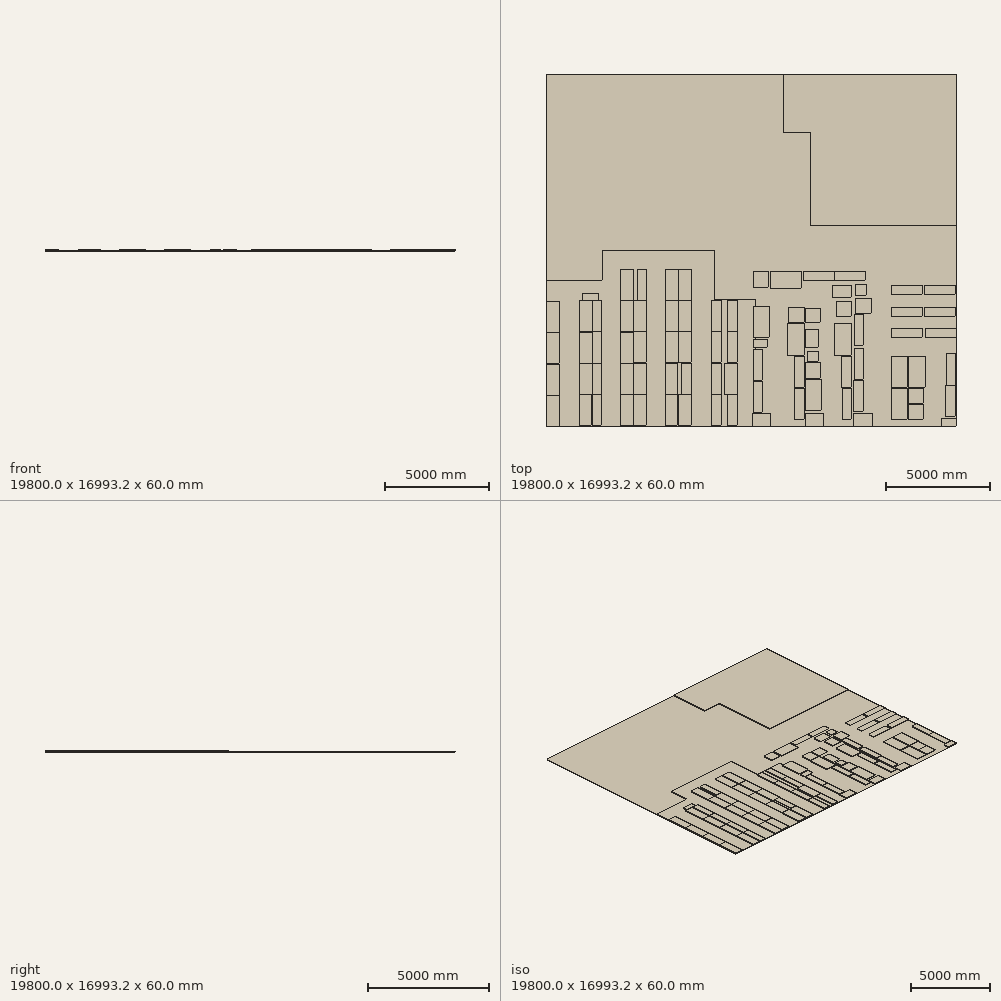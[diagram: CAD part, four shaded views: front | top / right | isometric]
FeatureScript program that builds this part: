
annotation { "Feature Type Name" : "Feature", "Feature Type Description" : "" }
export const myFeature = defineFeature(function(context is Context, id is Id, definition is map)
    precondition{}
    {
        {
            var Q0;
            Q0=qCreatedBy(makeId("Top.planeOp"),FACE);
            var sketch = newSketch(context, id + "F0", { "sketchPlane" : qUnion([Q0])});
            skLineSegment(sketch, "E0.bottom", {"start": v(9900, -8495) * mm, "end": v(-9900, -8495) * mm});
            skLineSegment(sketch, "E0.top", {"start": v(9900, 8495) * mm, "end": v(-9900, 8495) * mm});
            skLineSegment(sketch, "E0.left", {"start": v(9900, -8495) * mm, "end": v(9900, 8495) * mm});
            skLineSegment(sketch, "E0.right", {"start": v(-9900, -8495) * mm, "end": v(-9900, 8495) * mm});
            skPoint(sketch, "E0.middle", {"position": v(0, 0) * mm});
            skSolve(sketch);
        }
        {
            var Q0;
            Q0=qSketchRegion(id+"F0",true);
            extrude(context, id + "F1", {"entities" : qUnion([Q0]), "depth" : 10 * mm});
        }
        {
            var Q0;
            Q0=makeQuery(id+"F1.opExtrude","CAP_FACE",FACE,{"disambiguationData":[OSD([sQuery(id+"F0.wireOp",EDGE,"E0.bottom"),sQuery(id+"F0.wireOp",EDGE,"E0.top"),sQuery(id+"F0.wireOp",EDGE,"E0.left"),sQuery(id+"F0.wireOp",EDGE,"E0.right")])],"isStart":false});
            var sketch = newSketch(context, id + "F2", { "sketchPlane" : qUnion([Q0])});
            skLineSegment(sketch, "E1", {"start": v(-9900, -8495) * mm, "end": v(-9900, -1435) * mm});
            skLineSegment(sketch, "E2", {"start": v(-9900, -1435) * mm, "end": v(-7200, -1435) * mm});
            skLineSegment(sketch, "E3", {"start": v(-7200, -1435) * mm, "end": v(-7200, -5) * mm});
            skLineSegment(sketch, "E4", {"start": v(-7200, -5) * mm, "end": v(-1800, -5) * mm});
            skLineSegment(sketch, "E5", {"start": v(-1800, -5) * mm, "end": v(-1800, -2355) * mm});
            skLineSegment(sketch, "E6", {"start": v(-1800, -2355) * mm, "end": v(200, -2355) * mm});
            skLineSegment(sketch, "E7", {"start": v(200, -2355) * mm, "end": v(200, -8495) * mm});
            skLineSegment(sketch, "E8", {"start": v(200, -8495) * mm, "end": v(-9900, -8495) * mm});
            skLineSegment(sketch, "E9", {"start": v(9900, 1195) * mm, "end": v(9900, 8495) * mm});
            skLineSegment(sketch, "E10", {"start": v(9900, 8495) * mm, "end": v(1550, 8495) * mm});
            skLineSegment(sketch, "E11", {"start": v(1550, 8495) * mm, "end": v(1550, 5715) * mm});
            skLineSegment(sketch, "E12", {"start": v(1550, 5715) * mm, "end": v(2850, 5715) * mm});
            skLineSegment(sketch, "E13", {"start": v(2850, 5715) * mm, "end": v(2850, 1195) * mm});
            skLineSegment(sketch, "E14", {"start": v(2850, 1195) * mm, "end": v(9900, 1195) * mm});
            skLineSegment(sketch, "E15.left", {"start": v(3458.32, 469.72) * mm, "end": v(3008.32, 469.72) * mm});
            skPoint(sketch, "E15.middle", {"position": v(3233.32, -280.28) * mm});
            skLineSegment(sketch, "E16.left", {"start": v(4716.05, -36.44) * mm, "end": v(4096.05, -36.44) * mm});
            skPoint(sketch, "E16.middle", {"position": v(4406.05, -786.44) * mm});
            skSolve(sketch);
        }
        {
            var Q0;
            Q0=qSketchRegion(id+"F2",true);
            extrude(context, id + "F3", {"entities" : qUnion([Q0]), "operationType" : NewBodyOperationType.ADD, "depth" : 25 * mm});
        }
        {
            var Q0;
            Q0=makeQuery(id+"F3.opExtrude","CAP_FACE",FACE,{"disambiguationData":[OSD([sQuery(id+"F2.wireOp",EDGE,"E1"),sQuery(id+"F2.wireOp",EDGE,"E2"),sQuery(id+"F2.wireOp",EDGE,"E3"),sQuery(id+"F2.wireOp",EDGE,"E4"),sQuery(id+"F2.wireOp",EDGE,"E5"),sQuery(id+"F2.wireOp",EDGE,"E6"),sQuery(id+"F2.wireOp",EDGE,"E7"),sQuery(id+"F2.wireOp",EDGE,"E8")])],"isStart":false});
            var sketch = newSketch(context, id + "F4", { "sketchPlane" : qUnion([Q0])});
            skLineSegment(sketch, "E17.bottom", {"start": v(-9900, -8495) * mm, "end": v(-9900, -6995) * mm});
            skLineSegment(sketch, "E17.top", {"start": v(-9280, -8495) * mm, "end": v(-9280, -6995) * mm});
            skLineSegment(sketch, "E17.left", {"start": v(-9900, -8495) * mm, "end": v(-9280, -8495) * mm});
            skLineSegment(sketch, "E17.right", {"start": v(-9900, -6995) * mm, "end": v(-9280, -6995) * mm});
            skPoint(sketch, "E17.middle", {"position": v(-9590, -7745) * mm});
            skLineSegment(sketch, "E18.bottom", {"start": v(-9892.84, -6987.42) * mm, "end": v(-9892.84, -5487.42) * mm});
            skLineSegment(sketch, "E18.top", {"start": v(-9272.84, -6987.42) * mm, "end": v(-9272.84, -5487.42) * mm});
            skLineSegment(sketch, "E18.left", {"start": v(-9892.84, -6987.42) * mm, "end": v(-9272.84, -6987.42) * mm});
            skLineSegment(sketch, "E18.right", {"start": v(-9892.84, -5487.42) * mm, "end": v(-9272.84, -5487.42) * mm});
            skPoint(sketch, "E18.middle", {"position": v(-9582.84, -6237.42) * mm});
            skLineSegment(sketch, "E19.bottom", {"start": v(-9892.84, -5474.56) * mm, "end": v(-9892.84, -3974.56) * mm});
            skLineSegment(sketch, "E19.top", {"start": v(-9272.84, -5474.56) * mm, "end": v(-9272.84, -3974.56) * mm});
            skLineSegment(sketch, "E19.left", {"start": v(-9892.84, -5474.56) * mm, "end": v(-9272.84, -5474.56) * mm});
            skLineSegment(sketch, "E19.right", {"start": v(-9892.84, -3974.56) * mm, "end": v(-9272.84, -3974.56) * mm});
            skPoint(sketch, "E19.middle", {"position": v(-9582.84, -4724.56) * mm});
            skLineSegment(sketch, "E20.bottom", {"start": v(-9892.84, -3964.29) * mm, "end": v(-9892.84, -2464.29) * mm});
            skLineSegment(sketch, "E20.top", {"start": v(-9272.84, -3964.29) * mm, "end": v(-9272.84, -2464.29) * mm});
            skLineSegment(sketch, "E20.left", {"start": v(-9892.84, -3964.29) * mm, "end": v(-9272.84, -3964.29) * mm});
            skLineSegment(sketch, "E20.right", {"start": v(-9892.84, -2464.29) * mm, "end": v(-9272.84, -2464.29) * mm});
            skPoint(sketch, "E20.middle", {"position": v(-9582.84, -3214.29) * mm});
            skLineSegment(sketch, "E21.bottom", {"start": v(-8329.6, -8467.89) * mm, "end": v(-8329.6, -6967.89) * mm});
            skLineSegment(sketch, "E21.top", {"start": v(-7709.6, -8467.89) * mm, "end": v(-7709.6, -6967.89) * mm});
            skLineSegment(sketch, "E21.left", {"start": v(-8329.6, -8467.89) * mm, "end": v(-7709.6, -8467.89) * mm});
            skLineSegment(sketch, "E21.right", {"start": v(-8329.6, -6967.89) * mm, "end": v(-7709.6, -6967.89) * mm});
            skPoint(sketch, "E21.middle", {"position": v(-8019.6, -7717.89) * mm});
            skLineSegment(sketch, "E22.bottom", {"start": v(-8322.44, -6960.31) * mm, "end": v(-8322.44, -5460.31) * mm});
            skLineSegment(sketch, "E22.top", {"start": v(-7702.44, -6960.31) * mm, "end": v(-7702.44, -5460.31) * mm});
            skLineSegment(sketch, "E22.left", {"start": v(-8322.44, -6960.31) * mm, "end": v(-7702.44, -6960.31) * mm});
            skLineSegment(sketch, "E22.right", {"start": v(-8322.44, -5460.31) * mm, "end": v(-7702.44, -5460.31) * mm});
            skPoint(sketch, "E22.middle", {"position": v(-8012.44, -6210.31) * mm});
            skLineSegment(sketch, "E23.bottom", {"start": v(-8322.44, -5447.45) * mm, "end": v(-8322.44, -3947.45) * mm});
            skLineSegment(sketch, "E23.top", {"start": v(-7702.44, -5447.45) * mm, "end": v(-7702.44, -3947.45) * mm});
            skLineSegment(sketch, "E23.left", {"start": v(-8322.44, -5447.45) * mm, "end": v(-7702.44, -5447.45) * mm});
            skLineSegment(sketch, "E23.right", {"start": v(-8322.44, -3947.45) * mm, "end": v(-7702.44, -3947.45) * mm});
            skPoint(sketch, "E23.middle", {"position": v(-8012.44, -4697.45) * mm});
            skLineSegment(sketch, "E24.bottom", {"start": v(-8322.44, -3937.18) * mm, "end": v(-8322.44, -2437.18) * mm});
            skLineSegment(sketch, "E24.top", {"start": v(-7702.44, -3937.18) * mm, "end": v(-7702.44, -2437.18) * mm});
            skLineSegment(sketch, "E24.left", {"start": v(-8322.44, -3937.18) * mm, "end": v(-7702.44, -3937.18) * mm});
            skLineSegment(sketch, "E24.right", {"start": v(-8322.44, -2437.18) * mm, "end": v(-7702.44, -2437.18) * mm});
            skPoint(sketch, "E24.middle", {"position": v(-8012.44, -3187.18) * mm});
            skLineSegment(sketch, "E25.bottom", {"start": v(-7690, -8467.89) * mm, "end": v(-7690, -6967.89) * mm});
            skLineSegment(sketch, "E25.top", {"start": v(-7240, -8467.89) * mm, "end": v(-7240, -6967.89) * mm});
            skLineSegment(sketch, "E25.left", {"start": v(-7690, -8467.89) * mm, "end": v(-7240, -8467.89) * mm});
            skLineSegment(sketch, "E25.right", {"start": v(-7690, -6967.89) * mm, "end": v(-7240, -6967.89) * mm});
            skPoint(sketch, "E25.middle", {"position": v(-7465, -7717.89) * mm});
            skLineSegment(sketch, "E26.bottom", {"start": v(-7690, -6949.05) * mm, "end": v(-7690, -5449.05) * mm});
            skLineSegment(sketch, "E26.top", {"start": v(-7240, -6949.05) * mm, "end": v(-7240, -5449.05) * mm});
            skLineSegment(sketch, "E26.left", {"start": v(-7690, -6949.05) * mm, "end": v(-7240, -6949.05) * mm});
            skLineSegment(sketch, "E26.right", {"start": v(-7690, -5449.05) * mm, "end": v(-7240, -5449.05) * mm});
            skPoint(sketch, "E26.middle", {"position": v(-7465, -6199.05) * mm});
            skLineSegment(sketch, "E27.bottom", {"start": v(-7690, -5437.57) * mm, "end": v(-7690, -3937.57) * mm});
            skLineSegment(sketch, "E27.top", {"start": v(-7240, -5437.57) * mm, "end": v(-7240, -3937.57) * mm});
            skLineSegment(sketch, "E27.left", {"start": v(-7690, -5437.57) * mm, "end": v(-7240, -5437.57) * mm});
            skLineSegment(sketch, "E27.right", {"start": v(-7690, -3937.57) * mm, "end": v(-7240, -3937.57) * mm});
            skPoint(sketch, "E27.middle", {"position": v(-7465, -4687.57) * mm});
            skLineSegment(sketch, "E28.bottom", {"start": v(-7690, -3928.07) * mm, "end": v(-7690, -2428.07) * mm});
            skLineSegment(sketch, "E28.top", {"start": v(-7240, -3928.07) * mm, "end": v(-7240, -2428.07) * mm});
            skLineSegment(sketch, "E28.left", {"start": v(-7690, -3928.07) * mm, "end": v(-7240, -3928.07) * mm});
            skLineSegment(sketch, "E28.right", {"start": v(-7690, -2428.07) * mm, "end": v(-7240, -2428.07) * mm});
            skPoint(sketch, "E28.middle", {"position": v(-7465, -3178.07) * mm});
            skLineSegment(sketch, "E29.bottom", {"start": v(-8177.13, -2054.5) * mm, "end": v(-7388.6, -2054.5) * mm});
            skLineSegment(sketch, "E29.top", {"start": v(-8177.13, -2400.4) * mm, "end": v(-7388.6, -2400.4) * mm});
            skLineSegment(sketch, "E29.left", {"start": v(-8177.13, -2054.5) * mm, "end": v(-8177.13, -2400.4) * mm});
            skLineSegment(sketch, "E29.right", {"start": v(-7388.6, -2054.5) * mm, "end": v(-7388.6, -2400.4) * mm});
            skLineSegment(sketch, "E30.bottom", {"start": v(-6340, -8467.89) * mm, "end": v(-6340, -6967.89) * mm});
            skLineSegment(sketch, "E30.top", {"start": v(-5720, -8467.89) * mm, "end": v(-5720, -6967.89) * mm});
            skLineSegment(sketch, "E30.left", {"start": v(-6340, -8467.89) * mm, "end": v(-5720, -8467.89) * mm});
            skLineSegment(sketch, "E30.right", {"start": v(-6340, -6967.89) * mm, "end": v(-5720, -6967.89) * mm});
            skPoint(sketch, "E30.middle", {"position": v(-6030, -7717.89) * mm});
            skLineSegment(sketch, "E31.bottom", {"start": v(-6340, -6949.05) * mm, "end": v(-6340, -5449.05) * mm});
            skLineSegment(sketch, "E31.top", {"start": v(-5720, -6949.05) * mm, "end": v(-5720, -5449.05) * mm});
            skLineSegment(sketch, "E31.left", {"start": v(-6340, -6949.05) * mm, "end": v(-5720, -6949.05) * mm});
            skLineSegment(sketch, "E31.right", {"start": v(-6340, -5449.05) * mm, "end": v(-5720, -5449.05) * mm});
            skPoint(sketch, "E31.middle", {"position": v(-6030, -6199.05) * mm});
            skLineSegment(sketch, "E32.bottom", {"start": v(-6332.83, -5441.47) * mm, "end": v(-6332.83, -3941.47) * mm});
            skLineSegment(sketch, "E32.top", {"start": v(-5712.83, -5441.47) * mm, "end": v(-5712.83, -3941.47) * mm});
            skLineSegment(sketch, "E32.left", {"start": v(-6332.83, -5441.47) * mm, "end": v(-5712.83, -5441.47) * mm});
            skLineSegment(sketch, "E32.right", {"start": v(-6332.83, -3941.47) * mm, "end": v(-5712.83, -3941.47) * mm});
            skPoint(sketch, "E32.middle", {"position": v(-6022.83, -4691.47) * mm});
            skLineSegment(sketch, "E33.bottom", {"start": v(-6332.83, -3928.6) * mm, "end": v(-6332.83, -2428.6) * mm});
            skLineSegment(sketch, "E33.top", {"start": v(-5712.83, -3928.6) * mm, "end": v(-5712.83, -2428.6) * mm});
            skLineSegment(sketch, "E33.left", {"start": v(-6332.83, -3928.6) * mm, "end": v(-5712.83, -3928.6) * mm});
            skLineSegment(sketch, "E33.right", {"start": v(-6332.83, -2428.6) * mm, "end": v(-5712.83, -2428.6) * mm});
            skPoint(sketch, "E33.middle", {"position": v(-6022.83, -3178.6) * mm});
            skLineSegment(sketch, "E34.bottom", {"start": v(-6332.83, -2418.34) * mm, "end": v(-6332.83, -918.34) * mm});
            skLineSegment(sketch, "E34.top", {"start": v(-5712.83, -2418.34) * mm, "end": v(-5712.83, -918.34) * mm});
            skLineSegment(sketch, "E34.left", {"start": v(-6332.83, -2418.34) * mm, "end": v(-5712.83, -2418.34) * mm});
            skLineSegment(sketch, "E34.right", {"start": v(-6332.83, -918.34) * mm, "end": v(-5712.83, -918.34) * mm});
            skPoint(sketch, "E34.middle", {"position": v(-6022.83, -1668.34) * mm});
            skLineSegment(sketch, "E35.bottom", {"start": v(-5694.35, -8456.4) * mm, "end": v(-5694.35, -6956.4) * mm});
            skLineSegment(sketch, "E35.top", {"start": v(-5074.35, -8456.4) * mm, "end": v(-5074.35, -6956.4) * mm});
            skLineSegment(sketch, "E35.left", {"start": v(-5694.35, -8456.4) * mm, "end": v(-5074.35, -8456.4) * mm});
            skLineSegment(sketch, "E35.right", {"start": v(-5694.35, -6956.4) * mm, "end": v(-5074.35, -6956.4) * mm});
            skPoint(sketch, "E35.middle", {"position": v(-5384.35, -7706.4) * mm});
            skLineSegment(sketch, "E36.bottom", {"start": v(-5694.35, -6937.55) * mm, "end": v(-5694.35, -5437.55) * mm});
            skLineSegment(sketch, "E36.top", {"start": v(-5074.35, -6937.55) * mm, "end": v(-5074.35, -5437.55) * mm});
            skLineSegment(sketch, "E36.left", {"start": v(-5694.35, -6937.55) * mm, "end": v(-5074.35, -6937.55) * mm});
            skLineSegment(sketch, "E36.right", {"start": v(-5694.35, -5437.55) * mm, "end": v(-5074.35, -5437.55) * mm});
            skPoint(sketch, "E36.middle", {"position": v(-5384.35, -6187.55) * mm});
            skLineSegment(sketch, "E37.bottom", {"start": v(-5687.2, -5429.97) * mm, "end": v(-5687.2, -3929.97) * mm});
            skLineSegment(sketch, "E37.top", {"start": v(-5067.2, -5429.97) * mm, "end": v(-5067.2, -3929.97) * mm});
            skLineSegment(sketch, "E37.left", {"start": v(-5687.2, -5429.97) * mm, "end": v(-5067.2, -5429.97) * mm});
            skLineSegment(sketch, "E37.right", {"start": v(-5687.2, -3929.97) * mm, "end": v(-5067.2, -3929.97) * mm});
            skPoint(sketch, "E37.middle", {"position": v(-5377.2, -4679.97) * mm});
            skLineSegment(sketch, "E38.bottom", {"start": v(-5687.2, -3917.11) * mm, "end": v(-5687.2, -2417.11) * mm});
            skLineSegment(sketch, "E38.top", {"start": v(-5067.2, -3917.11) * mm, "end": v(-5067.2, -2417.11) * mm});
            skLineSegment(sketch, "E38.left", {"start": v(-5687.2, -3917.11) * mm, "end": v(-5067.2, -3917.11) * mm});
            skLineSegment(sketch, "E38.right", {"start": v(-5687.2, -2417.11) * mm, "end": v(-5067.2, -2417.11) * mm});
            skPoint(sketch, "E38.middle", {"position": v(-5377.2, -3167.11) * mm});
            skPoint(sketch, "E39.middle", {"position": v(-5377.2, -1656.84) * mm});
            skLineSegment(sketch, "E40.bottom", {"start": v(-5518.6, -2401.56) * mm, "end": v(-5518.6, -901.56) * mm});
            skLineSegment(sketch, "E40.top", {"start": v(-5068.6, -2401.56) * mm, "end": v(-5068.6, -901.56) * mm});
            skLineSegment(sketch, "E40.left", {"start": v(-5518.6, -2401.56) * mm, "end": v(-5068.6, -2401.56) * mm});
            skLineSegment(sketch, "E40.right", {"start": v(-5518.6, -901.56) * mm, "end": v(-5068.6, -901.56) * mm});
            skPoint(sketch, "E40.middle", {"position": v(-5293.6, -1651.56) * mm});
            skLineSegment(sketch, "E41.bottom", {"start": v(-4174.35, -8456.4) * mm, "end": v(-4174.35, -6956.4) * mm});
            skLineSegment(sketch, "E41.top", {"start": v(-3554.35, -8456.4) * mm, "end": v(-3554.35, -6956.4) * mm});
            skLineSegment(sketch, "E41.left", {"start": v(-4174.35, -8456.4) * mm, "end": v(-3554.35, -8456.4) * mm});
            skLineSegment(sketch, "E41.right", {"start": v(-4174.35, -6956.4) * mm, "end": v(-3554.35, -6956.4) * mm});
            skPoint(sketch, "E41.middle", {"position": v(-3864.35, -7706.4) * mm});
            skLineSegment(sketch, "E42.bottom", {"start": v(-4170.79, -6937.55) * mm, "end": v(-4170.79, -5437.55) * mm});
            skLineSegment(sketch, "E42.top", {"start": v(-3550.79, -6937.55) * mm, "end": v(-3550.79, -5437.55) * mm});
            skLineSegment(sketch, "E42.left", {"start": v(-4170.79, -6937.55) * mm, "end": v(-3550.79, -6937.55) * mm});
            skLineSegment(sketch, "E42.right", {"start": v(-4170.79, -5437.55) * mm, "end": v(-3550.79, -5437.55) * mm});
            skPoint(sketch, "E42.middle", {"position": v(-3860.79, -6187.55) * mm});
            skLineSegment(sketch, "E43.bottom", {"start": v(-4163.63, -5429.97) * mm, "end": v(-4163.63, -3929.97) * mm});
            skLineSegment(sketch, "E43.top", {"start": v(-3543.63, -5429.97) * mm, "end": v(-3543.63, -3929.97) * mm});
            skLineSegment(sketch, "E43.left", {"start": v(-4163.63, -5429.97) * mm, "end": v(-3543.63, -5429.97) * mm});
            skLineSegment(sketch, "E43.right", {"start": v(-4163.63, -3929.97) * mm, "end": v(-3543.63, -3929.97) * mm});
            skPoint(sketch, "E43.middle", {"position": v(-3853.63, -4679.97) * mm});
            skLineSegment(sketch, "E44.bottom", {"start": v(-4163.63, -3917.11) * mm, "end": v(-4163.63, -2417.11) * mm});
            skLineSegment(sketch, "E44.top", {"start": v(-3543.63, -3917.11) * mm, "end": v(-3543.63, -2417.11) * mm});
            skLineSegment(sketch, "E44.left", {"start": v(-4163.63, -3917.11) * mm, "end": v(-3543.63, -3917.11) * mm});
            skLineSegment(sketch, "E44.right", {"start": v(-4163.63, -2417.11) * mm, "end": v(-3543.63, -2417.11) * mm});
            skPoint(sketch, "E44.middle", {"position": v(-3853.63, -3167.11) * mm});
            skLineSegment(sketch, "E45.bottom", {"start": v(-4163.63, -2406.84) * mm, "end": v(-4163.63, -906.84) * mm});
            skLineSegment(sketch, "E45.top", {"start": v(-3543.63, -2406.84) * mm, "end": v(-3543.63, -906.84) * mm});
            skLineSegment(sketch, "E45.left", {"start": v(-4163.63, -2406.84) * mm, "end": v(-3543.63, -2406.84) * mm});
            skLineSegment(sketch, "E45.right", {"start": v(-4163.63, -906.84) * mm, "end": v(-3543.63, -906.84) * mm});
            skPoint(sketch, "E45.middle", {"position": v(-3853.63, -1656.84) * mm});
            skLineSegment(sketch, "E46.bottom", {"start": v(-3527.86, -8456.8) * mm, "end": v(-3527.86, -6956.8) * mm});
            skLineSegment(sketch, "E46.top", {"start": v(-2907.86, -8456.8) * mm, "end": v(-2907.86, -6956.8) * mm});
            skLineSegment(sketch, "E46.left", {"start": v(-3527.86, -8456.8) * mm, "end": v(-2907.86, -8456.8) * mm});
            skLineSegment(sketch, "E46.right", {"start": v(-3527.86, -6956.8) * mm, "end": v(-2907.86, -6956.8) * mm});
            skPoint(sketch, "E46.middle", {"position": v(-3217.86, -7706.8) * mm});
            skPoint(sketch, "E47.middle", {"position": v(-3214.3, -6187.96) * mm});
            skLineSegment(sketch, "E48.bottom", {"start": v(-3517.14, -5430.38) * mm, "end": v(-3517.14, -3930.38) * mm});
            skLineSegment(sketch, "E48.top", {"start": v(-2897.14, -5430.38) * mm, "end": v(-2897.14, -3930.38) * mm});
            skLineSegment(sketch, "E48.left", {"start": v(-3517.14, -5430.38) * mm, "end": v(-2897.14, -5430.38) * mm});
            skLineSegment(sketch, "E48.right", {"start": v(-3517.14, -3930.38) * mm, "end": v(-2897.14, -3930.38) * mm});
            skPoint(sketch, "E48.middle", {"position": v(-3207.14, -4680.38) * mm});
            skLineSegment(sketch, "E49.bottom", {"start": v(-3517.14, -3917.52) * mm, "end": v(-3517.14, -2417.52) * mm});
            skLineSegment(sketch, "E49.top", {"start": v(-2897.14, -3917.52) * mm, "end": v(-2897.14, -2417.52) * mm});
            skLineSegment(sketch, "E49.left", {"start": v(-3517.14, -3917.52) * mm, "end": v(-2897.14, -3917.52) * mm});
            skLineSegment(sketch, "E49.right", {"start": v(-3517.14, -2417.52) * mm, "end": v(-2897.14, -2417.52) * mm});
            skPoint(sketch, "E49.middle", {"position": v(-3207.14, -3167.52) * mm});
            skLineSegment(sketch, "E50.bottom", {"start": v(-3517.14, -2407.25) * mm, "end": v(-3517.14, -907.25) * mm});
            skLineSegment(sketch, "E50.top", {"start": v(-2897.14, -2407.25) * mm, "end": v(-2897.14, -907.25) * mm});
            skLineSegment(sketch, "E50.left", {"start": v(-3517.14, -2407.25) * mm, "end": v(-2897.14, -2407.25) * mm});
            skLineSegment(sketch, "E50.right", {"start": v(-3517.14, -907.25) * mm, "end": v(-2897.14, -907.25) * mm});
            skPoint(sketch, "E50.middle", {"position": v(-3207.14, -1657.25) * mm});
            skLineSegment(sketch, "E51.bottom", {"start": v(-3359.83, -6937.55) * mm, "end": v(-3359.83, -5437.55) * mm});
            skLineSegment(sketch, "E51.top", {"start": v(-2909.83, -6937.55) * mm, "end": v(-2909.83, -5437.55) * mm});
            skLineSegment(sketch, "E51.left", {"start": v(-3359.83, -6937.55) * mm, "end": v(-2909.83, -6937.55) * mm});
            skLineSegment(sketch, "E51.right", {"start": v(-3359.83, -5437.55) * mm, "end": v(-2909.83, -5437.55) * mm});
            skPoint(sketch, "E51.middle", {"position": v(-3134.83, -6187.55) * mm});
            skLineSegment(sketch, "E52.bottom", {"start": v(-1907.64, -8456.4) * mm, "end": v(-1907.64, -6956.4) * mm});
            skLineSegment(sketch, "E52.top", {"start": v(-1457.64, -8456.4) * mm, "end": v(-1457.64, -6956.4) * mm});
            skLineSegment(sketch, "E52.left", {"start": v(-1907.64, -8456.4) * mm, "end": v(-1457.64, -8456.4) * mm});
            skLineSegment(sketch, "E52.right", {"start": v(-1907.64, -6956.4) * mm, "end": v(-1457.64, -6956.4) * mm});
            skPoint(sketch, "E52.middle", {"position": v(-1682.64, -7706.4) * mm});
            skLineSegment(sketch, "E53.bottom", {"start": v(-1907.64, -6937.55) * mm, "end": v(-1907.64, -5437.55) * mm});
            skLineSegment(sketch, "E53.top", {"start": v(-1457.64, -6937.55) * mm, "end": v(-1457.64, -5437.55) * mm});
            skLineSegment(sketch, "E53.left", {"start": v(-1907.64, -6937.55) * mm, "end": v(-1457.64, -6937.55) * mm});
            skLineSegment(sketch, "E53.right", {"start": v(-1907.64, -5437.55) * mm, "end": v(-1457.64, -5437.55) * mm});
            skPoint(sketch, "E53.middle", {"position": v(-1682.64, -6187.55) * mm});
            skLineSegment(sketch, "E54.bottom", {"start": v(-1907.64, -5429.98) * mm, "end": v(-1907.64, -3929.98) * mm});
            skLineSegment(sketch, "E54.top", {"start": v(-1457.64, -5429.98) * mm, "end": v(-1457.64, -3929.98) * mm});
            skLineSegment(sketch, "E54.left", {"start": v(-1907.64, -5429.98) * mm, "end": v(-1457.64, -5429.98) * mm});
            skLineSegment(sketch, "E54.right", {"start": v(-1907.64, -3929.98) * mm, "end": v(-1457.64, -3929.98) * mm});
            skPoint(sketch, "E54.middle", {"position": v(-1682.64, -4679.98) * mm});
            skLineSegment(sketch, "E55.bottom", {"start": v(-1907.64, -3917.11) * mm, "end": v(-1907.64, -2417.11) * mm});
            skLineSegment(sketch, "E55.top", {"start": v(-1457.64, -3917.11) * mm, "end": v(-1457.64, -2417.11) * mm});
            skLineSegment(sketch, "E55.left", {"start": v(-1907.64, -3917.11) * mm, "end": v(-1457.64, -3917.11) * mm});
            skLineSegment(sketch, "E55.right", {"start": v(-1907.64, -2417.11) * mm, "end": v(-1457.64, -2417.11) * mm});
            skPoint(sketch, "E55.middle", {"position": v(-1682.64, -3167.11) * mm});
            skLineSegment(sketch, "E56.bottom", {"start": v(-1149.63, -8456.4) * mm, "end": v(-1149.63, -6956.4) * mm});
            skLineSegment(sketch, "E56.top", {"start": v(-699.63, -8456.4) * mm, "end": v(-699.63, -6956.4) * mm});
            skLineSegment(sketch, "E56.left", {"start": v(-1149.63, -8456.4) * mm, "end": v(-699.63, -8456.4) * mm});
            skLineSegment(sketch, "E56.right", {"start": v(-1149.63, -6956.4) * mm, "end": v(-699.63, -6956.4) * mm});
            skPoint(sketch, "E56.middle", {"position": v(-924.63, -7706.4) * mm});
            skLineSegment(sketch, "E57.bottom", {"start": v(-1318.62, -6937.55) * mm, "end": v(-1318.62, -5437.55) * mm});
            skLineSegment(sketch, "E57.top", {"start": v(-698.62, -6937.55) * mm, "end": v(-698.62, -5437.55) * mm});
            skLineSegment(sketch, "E57.left", {"start": v(-1318.62, -6937.55) * mm, "end": v(-698.62, -6937.55) * mm});
            skPoint(sketch, "E57.middle", {"position": v(-1008.62, -6187.55) * mm});
            skLineSegment(sketch, "E58", {"start": v(-1318.62, -5437.55) * mm, "end": v(-698.62, -5437.55) * mm});
            skLineSegment(sketch, "E59.right", {"start": v(-1149.63, -5429.98) * mm, "end": v(-699.63, -5429.98) * mm});
            skLineSegment(sketch, "E60.bottom", {"start": v(-1149.63, -5422.4) * mm, "end": v(-1149.63, -3922.4) * mm});
            skLineSegment(sketch, "E60.top", {"start": v(-699.63, -5422.4) * mm, "end": v(-699.63, -3922.4) * mm});
            skLineSegment(sketch, "E60.left", {"start": v(-1149.63, -5422.4) * mm, "end": v(-699.63, -5422.4) * mm});
            skLineSegment(sketch, "E60.right", {"start": v(-1149.63, -3922.4) * mm, "end": v(-699.63, -3922.4) * mm});
            skPoint(sketch, "E60.middle", {"position": v(-924.63, -4672.4) * mm});
            skLineSegment(sketch, "E61.bottom", {"start": v(-1149.63, -3909.54) * mm, "end": v(-1149.63, -2409.54) * mm});
            skLineSegment(sketch, "E61.top", {"start": v(-699.63, -3909.54) * mm, "end": v(-699.63, -2409.54) * mm});
            skLineSegment(sketch, "E61.left", {"start": v(-1149.63, -3909.54) * mm, "end": v(-699.63, -3909.54) * mm});
            skLineSegment(sketch, "E61.right", {"start": v(-1149.63, -2409.54) * mm, "end": v(-699.63, -2409.54) * mm});
            skPoint(sketch, "E61.middle", {"position": v(-924.63, -3159.54) * mm});
            skLineSegment(sketch, "E62.bottom", {"start": v(5025.03, -2298.58) * mm, "end": v(5775.03, -2298.58) * mm});
            skLineSegment(sketch, "E62.top", {"start": v(5025.03, -3048.58) * mm, "end": v(5775.03, -3048.58) * mm});
            skLineSegment(sketch, "E62.left", {"start": v(5025.03, -2298.58) * mm, "end": v(5025.03, -3048.58) * mm});
            skLineSegment(sketch, "E62.right", {"start": v(5775.03, -2298.58) * mm, "end": v(5775.03, -3048.58) * mm});
            skLineSegment(sketch, "E63.bottom", {"start": v(30, -7895) * mm, "end": v(930, -7895) * mm});
            skLineSegment(sketch, "E63.top", {"start": v(30, -8495) * mm, "end": v(930, -8495) * mm});
            skLineSegment(sketch, "E63.left", {"start": v(30, -7895) * mm, "end": v(30, -8495) * mm});
            skLineSegment(sketch, "E63.right", {"start": v(930, -7895) * mm, "end": v(930, -8495) * mm});
            skLineSegment(sketch, "E64.bottom", {"start": v(76.53, -7825) * mm, "end": v(76.53, -6325) * mm});
            skLineSegment(sketch, "E64.top", {"start": v(526.53, -7825) * mm, "end": v(526.53, -6325) * mm});
            skLineSegment(sketch, "E64.left", {"start": v(76.53, -7825) * mm, "end": v(526.53, -7825) * mm});
            skLineSegment(sketch, "E64.right", {"start": v(76.53, -6325) * mm, "end": v(526.53, -6325) * mm});
            skLineSegment(sketch, "E65.bottom", {"start": v(76.53, -6276.16) * mm, "end": v(76.53, -4776.16) * mm});
            skLineSegment(sketch, "E65.top", {"start": v(526.53, -6276.16) * mm, "end": v(526.53, -4776.16) * mm});
            skLineSegment(sketch, "E65.left", {"start": v(76.53, -6276.16) * mm, "end": v(526.53, -6276.16) * mm});
            skLineSegment(sketch, "E65.right", {"start": v(76.53, -4776.16) * mm, "end": v(526.53, -4776.16) * mm});
            skLineSegment(sketch, "E66.bottom", {"start": v(76.53, -1019.37) * mm, "end": v(826.53, -1019.37) * mm});
            skLineSegment(sketch, "E66.top", {"start": v(76.53, -1769.37) * mm, "end": v(826.53, -1769.37) * mm});
            skLineSegment(sketch, "E66.left", {"start": v(76.53, -1019.37) * mm, "end": v(76.53, -1769.37) * mm});
            skLineSegment(sketch, "E66.right", {"start": v(826.53, -1019.37) * mm, "end": v(826.53, -1769.37) * mm});
            skLineSegment(sketch, "E67.bottom", {"start": v(2424.2, -1019.37) * mm, "end": v(2424.2, -1819.37) * mm});
            skLineSegment(sketch, "E67.top", {"start": v(924.2, -1019.37) * mm, "end": v(924.2, -1819.37) * mm});
            skLineSegment(sketch, "E67.left", {"start": v(2424.2, -1019.37) * mm, "end": v(924.2, -1019.37) * mm});
            skLineSegment(sketch, "E67.right", {"start": v(2424.2, -1819.37) * mm, "end": v(924.2, -1819.37) * mm});
            skLineSegment(sketch, "E68.bottom", {"start": v(2491.14, -1019.37) * mm, "end": v(3991.14, -1019.37) * mm});
            skLineSegment(sketch, "E68.top", {"start": v(2491.14, -1469.37) * mm, "end": v(3991.14, -1469.37) * mm});
            skLineSegment(sketch, "E68.left", {"start": v(2491.14, -1019.37) * mm, "end": v(2491.14, -1469.37) * mm});
            skLineSegment(sketch, "E68.right", {"start": v(3991.14, -1019.37) * mm, "end": v(3991.14, -1469.37) * mm});
            skLineSegment(sketch, "E69.bottom", {"start": v(4021.14, -1019.37) * mm, "end": v(5521.14, -1019.37) * mm});
            skLineSegment(sketch, "E69.top", {"start": v(4021.14, -1469.37) * mm, "end": v(5521.14, -1469.37) * mm});
            skLineSegment(sketch, "E69.left", {"start": v(4021.14, -1019.37) * mm, "end": v(4021.14, -1469.37) * mm});
            skLineSegment(sketch, "E69.right", {"start": v(5521.14, -1019.37) * mm, "end": v(5521.14, -1469.37) * mm});
            skLineSegment(sketch, "E70.bottom", {"start": v(1787.35, -2748.15) * mm, "end": v(2537.35, -2748.15) * mm});
            skLineSegment(sketch, "E70.top", {"start": v(1787.35, -3498.15) * mm, "end": v(2537.35, -3498.15) * mm});
            skLineSegment(sketch, "E70.left", {"start": v(1787.35, -2748.15) * mm, "end": v(1787.35, -3498.15) * mm});
            skLineSegment(sketch, "E70.right", {"start": v(2537.35, -2748.15) * mm, "end": v(2537.35, -3498.15) * mm});
            skLineSegment(sketch, "E71.bottom", {"start": v(1737.35, -3548.58) * mm, "end": v(2537.35, -3548.58) * mm});
            skLineSegment(sketch, "E71.top", {"start": v(1737.35, -5048.58) * mm, "end": v(2537.35, -5048.58) * mm});
            skLineSegment(sketch, "E71.left", {"start": v(1737.35, -3548.58) * mm, "end": v(1737.35, -5048.58) * mm});
            skLineSegment(sketch, "E71.right", {"start": v(2537.35, -3548.58) * mm, "end": v(2537.35, -5048.58) * mm});
            skLineSegment(sketch, "E72.bottom", {"start": v(2099.98, -8187) * mm, "end": v(2099.98, -6687) * mm});
            skLineSegment(sketch, "E72.top", {"start": v(2549.98, -8187) * mm, "end": v(2549.98, -6687) * mm});
            skLineSegment(sketch, "E72.left", {"start": v(2099.98, -8187) * mm, "end": v(2549.98, -8187) * mm});
            skLineSegment(sketch, "E72.right", {"start": v(2099.98, -6687) * mm, "end": v(2549.98, -6687) * mm});
            skLineSegment(sketch, "E73.bottom", {"start": v(2092.87, -6621.47) * mm, "end": v(2092.87, -5121.47) * mm});
            skLineSegment(sketch, "E73.top", {"start": v(2542.87, -6621.47) * mm, "end": v(2542.87, -5121.47) * mm});
            skLineSegment(sketch, "E73.left", {"start": v(2092.87, -6621.47) * mm, "end": v(2542.87, -6621.47) * mm});
            skLineSegment(sketch, "E73.right", {"start": v(2092.87, -5121.47) * mm, "end": v(2542.87, -5121.47) * mm});
            skLineSegment(sketch, "E74.bottom", {"start": v(2589.98, -7895) * mm, "end": v(3489.98, -7895) * mm});
            skLineSegment(sketch, "E74.top", {"start": v(2589.98, -8495) * mm, "end": v(3489.98, -8495) * mm});
            skLineSegment(sketch, "E74.left", {"start": v(2589.98, -7895) * mm, "end": v(2589.98, -8495) * mm});
            skLineSegment(sketch, "E74.right", {"start": v(3489.98, -7895) * mm, "end": v(3489.98, -8495) * mm});
            skLineSegment(sketch, "E75.bottom", {"start": v(2589.98, -5426.16) * mm, "end": v(3339.98, -5426.16) * mm});
            skLineSegment(sketch, "E75.top", {"start": v(2589.98, -6176.16) * mm, "end": v(3339.98, -6176.16) * mm});
            skLineSegment(sketch, "E75.left", {"start": v(2589.98, -5426.16) * mm, "end": v(2589.98, -6176.16) * mm});
            skLineSegment(sketch, "E75.right", {"start": v(3339.98, -5426.16) * mm, "end": v(3339.98, -6176.16) * mm});
            skLineSegment(sketch, "E76.bottom", {"start": v(5040.1, -1663) * mm, "end": v(5540.1, -1663) * mm});
            skLineSegment(sketch, "E76.top", {"start": v(5040.1, -2163) * mm, "end": v(5540.1, -2163) * mm});
            skLineSegment(sketch, "E76.left", {"start": v(5040.1, -1663) * mm, "end": v(5040.1, -2163) * mm});
            skLineSegment(sketch, "E76.right", {"start": v(5540.1, -1663) * mm, "end": v(5540.1, -2163) * mm});
            skLineSegment(sketch, "E77.bottom", {"start": v(2715.73, -4861.47) * mm, "end": v(3215.73, -4861.47) * mm});
            skLineSegment(sketch, "E77.top", {"start": v(2715.73, -5361.47) * mm, "end": v(3215.73, -5361.47) * mm});
            skLineSegment(sketch, "E77.left", {"start": v(2715.73, -4861.47) * mm, "end": v(2715.73, -5361.47) * mm});
            skLineSegment(sketch, "E77.right", {"start": v(3215.73, -4861.47) * mm, "end": v(3215.73, -5361.47) * mm});
            skLineSegment(sketch, "E78.bottom", {"start": v(2589.98, -2798.58) * mm, "end": v(3339.98, -2798.58) * mm});
            skLineSegment(sketch, "E78.top", {"start": v(2589.98, -3498.15) * mm, "end": v(3339.98, -3498.15) * mm});
            skLineSegment(sketch, "E78.left", {"start": v(2589.98, -2748.15) * mm, "end": v(2589.98, -3498.15) * mm});
            skLineSegment(sketch, "E78.right", {"start": v(3339.98, -2748.15) * mm, "end": v(3339.98, -3498.15) * mm});
            skLineSegment(sketch, "E79.bottom", {"start": v(2589.98, -6245) * mm, "end": v(3389.98, -6245) * mm});
            skLineSegment(sketch, "E79.top", {"start": v(2589.98, -7745) * mm, "end": v(3389.98, -7745) * mm});
            skLineSegment(sketch, "E79.left", {"start": v(2589.98, -6245) * mm, "end": v(2589.98, -7745) * mm});
            skLineSegment(sketch, "E79.right", {"start": v(3389.98, -6245) * mm, "end": v(3389.98, -7745) * mm});
            skLineSegment(sketch, "E80.bottom", {"start": v(3225.45, -3797.34) * mm, "end": v(3225.45, -4697.34) * mm});
            skLineSegment(sketch, "E80.top", {"start": v(2625.45, -3797.34) * mm, "end": v(2625.45, -4697.34) * mm});
            skLineSegment(sketch, "E80.left", {"start": v(3225.45, -3797.34) * mm, "end": v(2625.45, -3797.34) * mm});
            skLineSegment(sketch, "E80.right", {"start": v(3225.45, -4697.34) * mm, "end": v(2625.45, -4697.34) * mm});
            skLineSegment(sketch, "E81.bottom", {"start": v(3935.03, -1683) * mm, "end": v(4835.03, -1683) * mm});
            skLineSegment(sketch, "E81.top", {"start": v(3935.03, -2283) * mm, "end": v(4835.03, -2283) * mm});
            skLineSegment(sketch, "E81.left", {"start": v(3935.03, -1683) * mm, "end": v(3935.03, -2283) * mm});
            skLineSegment(sketch, "E81.right", {"start": v(4835.03, -1683) * mm, "end": v(4835.03, -2283) * mm});
            skLineSegment(sketch, "E82.bottom", {"start": v(4099.25, -2448.14) * mm, "end": v(4849.25, -2448.14) * mm});
            skLineSegment(sketch, "E82.top", {"start": v(4099.25, -3198.14) * mm, "end": v(4849.25, -3198.14) * mm});
            skLineSegment(sketch, "E82.left", {"start": v(4099.25, -2448.14) * mm, "end": v(4099.25, -3198.14) * mm});
            skLineSegment(sketch, "E82.right", {"start": v(4849.25, -2448.14) * mm, "end": v(4849.25, -3198.14) * mm});
            skLineSegment(sketch, "E83.bottom", {"start": v(4021.25, -3548.58) * mm, "end": v(4821.25, -3548.58) * mm});
            skLineSegment(sketch, "E83.top", {"start": v(4021.25, -5048.58) * mm, "end": v(4821.25, -5048.58) * mm});
            skLineSegment(sketch, "E83.left", {"start": v(4021.25, -3548.58) * mm, "end": v(4021.25, -5048.58) * mm});
            skLineSegment(sketch, "E83.right", {"start": v(4821.25, -3548.58) * mm, "end": v(4821.25, -5048.58) * mm});
            skLineSegment(sketch, "E84.bottom", {"start": v(4380.02, -8187) * mm, "end": v(4380.02, -6687) * mm});
            skLineSegment(sketch, "E84.top", {"start": v(4830.02, -8187) * mm, "end": v(4830.02, -6687) * mm});
            skLineSegment(sketch, "E84.left", {"start": v(4380.02, -8187) * mm, "end": v(4830.02, -8187) * mm});
            skLineSegment(sketch, "E84.right", {"start": v(4380.02, -6687) * mm, "end": v(4830.02, -6687) * mm});
            skLineSegment(sketch, "E85.bottom", {"start": v(4356.8, -6603.54) * mm, "end": v(4356.8, -5103.54) * mm});
            skLineSegment(sketch, "E85.top", {"start": v(4806.8, -6603.54) * mm, "end": v(4806.8, -5103.54) * mm});
            skLineSegment(sketch, "E85.left", {"start": v(4356.8, -6603.54) * mm, "end": v(4806.8, -6603.54) * mm});
            skLineSegment(sketch, "E85.right", {"start": v(4356.8, -5103.54) * mm, "end": v(4806.8, -5103.54) * mm});
            skLineSegment(sketch, "E86.bottom", {"start": v(4954.69, -4598.1) * mm, "end": v(4954.69, -3098.1) * mm});
            skLineSegment(sketch, "E86.top", {"start": v(5404.69, -4598.1) * mm, "end": v(5404.69, -3098.1) * mm});
            skLineSegment(sketch, "E86.left", {"start": v(4954.69, -4598.1) * mm, "end": v(5404.69, -4598.1) * mm});
            skLineSegment(sketch, "E86.right", {"start": v(4954.69, -3098.1) * mm, "end": v(5404.69, -3098.1) * mm});
            skLineSegment(sketch, "E87.bottom", {"start": v(4954.69, -6237.65) * mm, "end": v(4954.69, -4737.65) * mm});
            skLineSegment(sketch, "E87.top", {"start": v(5404.69, -6237.65) * mm, "end": v(5404.69, -4737.65) * mm});
            skLineSegment(sketch, "E87.left", {"start": v(4954.69, -6237.65) * mm, "end": v(5404.69, -6237.65) * mm});
            skLineSegment(sketch, "E87.right", {"start": v(4954.69, -4737.65) * mm, "end": v(5404.69, -4737.65) * mm});
            skLineSegment(sketch, "E88.bottom", {"start": v(4937.88, -7785) * mm, "end": v(4937.88, -6285) * mm});
            skLineSegment(sketch, "E88.top", {"start": v(5387.88, -7785) * mm, "end": v(5387.88, -6285) * mm});
            skLineSegment(sketch, "E88.left", {"start": v(4937.88, -7785) * mm, "end": v(5387.88, -7785) * mm});
            skLineSegment(sketch, "E88.right", {"start": v(4937.88, -6285) * mm, "end": v(5387.88, -6285) * mm});
            skLineSegment(sketch, "E89.bottom", {"start": v(4937.88, -7895) * mm, "end": v(5837.88, -7895) * mm});
            skLineSegment(sketch, "E89.top", {"start": v(4937.88, -8495) * mm, "end": v(5837.88, -8495) * mm});
            skLineSegment(sketch, "E89.left", {"start": v(4937.88, -7895) * mm, "end": v(4937.88, -8495) * mm});
            skLineSegment(sketch, "E89.right", {"start": v(5837.88, -7895) * mm, "end": v(5837.88, -8495) * mm});
            skLineSegment(sketch, "E90.bottom", {"start": v(6737.4, -6678.23) * mm, "end": v(7537.4, -6678.23) * mm});
            skLineSegment(sketch, "E90.top", {"start": v(6737.4, -8178.23) * mm, "end": v(7537.4, -8178.23) * mm});
            skLineSegment(sketch, "E90.left", {"start": v(6737.4, -6678.23) * mm, "end": v(6737.4, -8178.23) * mm});
            skLineSegment(sketch, "E90.right", {"start": v(7537.4, -6678.23) * mm, "end": v(7537.4, -8178.23) * mm});
            skLineSegment(sketch, "E91.bottom", {"start": v(6737.4, -5103.54) * mm, "end": v(7537.4, -5103.54) * mm});
            skLineSegment(sketch, "E91.top", {"start": v(6737.4, -6603.54) * mm, "end": v(7537.4, -6603.54) * mm});
            skLineSegment(sketch, "E91.left", {"start": v(6737.4, -5103.54) * mm, "end": v(6737.4, -6603.54) * mm});
            skLineSegment(sketch, "E91.right", {"start": v(7537.4, -5103.54) * mm, "end": v(7537.4, -6603.54) * mm});
            skLineSegment(sketch, "E92.bottom", {"start": v(9391.63, -8030.62) * mm, "end": v(9391.63, -6530.62) * mm});
            skLineSegment(sketch, "E92.top", {"start": v(9841.63, -8030.62) * mm, "end": v(9841.63, -6530.62) * mm});
            skLineSegment(sketch, "E92.left", {"start": v(9391.63, -8030.62) * mm, "end": v(9841.63, -8030.62) * mm});
            skLineSegment(sketch, "E92.right", {"start": v(9391.63, -6530.62) * mm, "end": v(9841.63, -6530.62) * mm});
            skLineSegment(sketch, "E93.bottom", {"start": v(9414.44, -6498.29) * mm, "end": v(9414.44, -4998.29) * mm});
            skLineSegment(sketch, "E93.top", {"start": v(9864.44, -6498.29) * mm, "end": v(9864.44, -4998.29) * mm});
            skLineSegment(sketch, "E93.left", {"start": v(9414.44, -6498.29) * mm, "end": v(9864.44, -6498.29) * mm});
            skLineSegment(sketch, "E93.right", {"start": v(9414.44, -4998.29) * mm, "end": v(9864.44, -4998.29) * mm});
            skLineSegment(sketch, "E94.bottom", {"start": v(7577.4, -7428.23) * mm, "end": v(8327.4, -7428.23) * mm});
            skLineSegment(sketch, "E94.top", {"start": v(7577.4, -8178.23) * mm, "end": v(8327.4, -8178.23) * mm});
            skLineSegment(sketch, "E94.left", {"start": v(7577.4, -7428.23) * mm, "end": v(7577.4, -8178.23) * mm});
            skLineSegment(sketch, "E94.right", {"start": v(8327.4, -7428.23) * mm, "end": v(8327.4, -8178.23) * mm});
            skLineSegment(sketch, "E95.bottom", {"start": v(7577.4, -6650.63) * mm, "end": v(8327.4, -6650.63) * mm});
            skLineSegment(sketch, "E95.top", {"start": v(7577.4, -7400.63) * mm, "end": v(8327.4, -7400.63) * mm});
            skLineSegment(sketch, "E95.left", {"start": v(7577.4, -6650.63) * mm, "end": v(7577.4, -7400.63) * mm});
            skLineSegment(sketch, "E95.right", {"start": v(8327.4, -6650.63) * mm, "end": v(8327.4, -7400.63) * mm});
            skLineSegment(sketch, "E96.bottom", {"start": v(7587.14, -5103.54) * mm, "end": v(8387.14, -5103.54) * mm});
            skLineSegment(sketch, "E96.top", {"start": v(7587.14, -6603.54) * mm, "end": v(8387.14, -6603.54) * mm});
            skLineSegment(sketch, "E96.left", {"start": v(7587.14, -5103.54) * mm, "end": v(7587.14, -6603.54) * mm});
            skLineSegment(sketch, "E96.right", {"start": v(8387.14, -5103.54) * mm, "end": v(8387.14, -6603.54) * mm});
            skLineSegment(sketch, "E97.bottom", {"start": v(9188.03, -8098.25) * mm, "end": v(9888.03, -8098.25) * mm});
            skLineSegment(sketch, "E97.top", {"start": v(9188.03, -8498.25) * mm, "end": v(9888.03, -8498.25) * mm});
            skLineSegment(sketch, "E97.left", {"start": v(9188.03, -8098.25) * mm, "end": v(9188.03, -8498.25) * mm});
            skLineSegment(sketch, "E97.right", {"start": v(9888.03, -8098.25) * mm, "end": v(9888.03, -8498.25) * mm});
            skLineSegment(sketch, "E98.bottom", {"start": v(9841.63, -2141.79) * mm, "end": v(8341.63, -2141.79) * mm});
            skLineSegment(sketch, "E98.top", {"start": v(9841.63, -1691.79) * mm, "end": v(8341.63, -1691.79) * mm});
            skLineSegment(sketch, "E98.left", {"start": v(9841.63, -2141.79) * mm, "end": v(9841.63, -1691.79) * mm});
            skLineSegment(sketch, "E98.right", {"start": v(8341.63, -2141.79) * mm, "end": v(8341.63, -1691.79) * mm});
            skLineSegment(sketch, "E99.bottom", {"start": v(8237.4, -2141.79) * mm, "end": v(6737.4, -2141.79) * mm});
            skLineSegment(sketch, "E99.top", {"start": v(8237.4, -1691.79) * mm, "end": v(6737.4, -1691.79) * mm});
            skLineSegment(sketch, "E99.left", {"start": v(8237.4, -2141.79) * mm, "end": v(8237.4, -1691.79) * mm});
            skLineSegment(sketch, "E99.right", {"start": v(6737.4, -2141.79) * mm, "end": v(6737.4, -1691.79) * mm});
            skLineSegment(sketch, "E100.bottom", {"start": v(9841.63, -3183.43) * mm, "end": v(8341.63, -3183.43) * mm});
            skLineSegment(sketch, "E100.top", {"start": v(9841.63, -2733.43) * mm, "end": v(8341.63, -2733.43) * mm});
            skLineSegment(sketch, "E100.left", {"start": v(9841.63, -3183.43) * mm, "end": v(9841.63, -2733.43) * mm});
            skLineSegment(sketch, "E100.right", {"start": v(8341.63, -3183.43) * mm, "end": v(8341.63, -2733.43) * mm});
            skLineSegment(sketch, "E101.bottom", {"start": v(8237.4, -3183.43) * mm, "end": v(6737.4, -3183.43) * mm});
            skLineSegment(sketch, "E101.top", {"start": v(8237.4, -2733.43) * mm, "end": v(6737.4, -2733.43) * mm});
            skLineSegment(sketch, "E101.left", {"start": v(8237.4, -3183.43) * mm, "end": v(8237.4, -2733.43) * mm});
            skLineSegment(sketch, "E101.right", {"start": v(6737.4, -3183.43) * mm, "end": v(6737.4, -2733.43) * mm});
            skLineSegment(sketch, "E102.bottom", {"start": v(9887.14, -4221.52) * mm, "end": v(8387.14, -4221.52) * mm});
            skLineSegment(sketch, "E102.top", {"start": v(9887.14, -3771.52) * mm, "end": v(8387.14, -3771.52) * mm});
            skLineSegment(sketch, "E102.left", {"start": v(9887.14, -4221.52) * mm, "end": v(9887.14, -3771.52) * mm});
            skLineSegment(sketch, "E102.right", {"start": v(8387.14, -4221.52) * mm, "end": v(8387.14, -3771.52) * mm});
            skLineSegment(sketch, "E103.bottom", {"start": v(8237.4, -4221) * mm, "end": v(6737.4, -4221) * mm});
            skLineSegment(sketch, "E103.top", {"start": v(8237.4, -3771) * mm, "end": v(6737.4, -3771) * mm});
            skLineSegment(sketch, "E103.left", {"start": v(8237.4, -4221) * mm, "end": v(8237.4, -3771) * mm});
            skLineSegment(sketch, "E103.right", {"start": v(6737.4, -4221) * mm, "end": v(6737.4, -3771) * mm});
            skLineSegment(sketch, "E104.bottom", {"start": v(79.53, -4297.34) * mm, "end": v(779.53, -4297.34) * mm});
            skLineSegment(sketch, "E104.top", {"start": v(79.53, -4697.34) * mm, "end": v(779.53, -4697.34) * mm});
            skLineSegment(sketch, "E104.left", {"start": v(79.53, -4297.34) * mm, "end": v(79.53, -4697.34) * mm});
            skLineSegment(sketch, "E104.right", {"start": v(779.53, -4297.34) * mm, "end": v(779.53, -4697.34) * mm});
            skLineSegment(sketch, "E105.bottom", {"start": v(85, -2706.35) * mm, "end": v(885, -2706.35) * mm});
            skLineSegment(sketch, "E105.top", {"start": v(85, -4206.35) * mm, "end": v(885, -4206.35) * mm});
            skLineSegment(sketch, "E105.left", {"start": v(85, -2706.35) * mm, "end": v(85, -4206.35) * mm});
            skLineSegment(sketch, "E105.right", {"start": v(885, -2706.35) * mm, "end": v(885, -4206.35) * mm});
            skSolve(sketch);
        }
        {
            var Q0;
            Q0=qSketchRegion(id+"F4",true);
            extrude(context, id + "F5", {"entities" : qUnion([Q0]), "depth" : 25 * mm});
        }
    });
